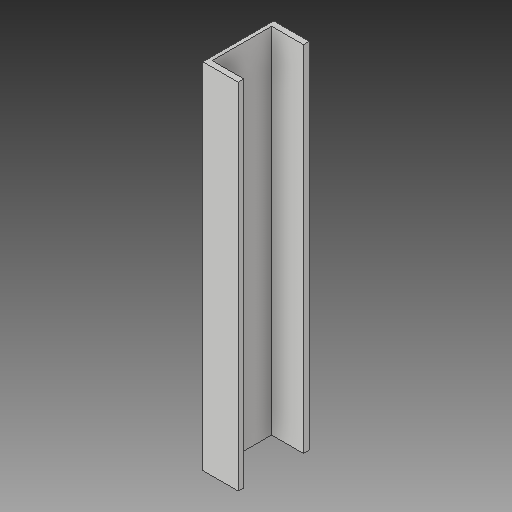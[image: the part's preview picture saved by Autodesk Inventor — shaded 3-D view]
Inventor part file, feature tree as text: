
AUTODESK INVENTOR PART (.ipt)
format: ipt  version: 2019 (Build 230136000, 136)  size: 88,064 bytes
history: native  units: in
note: dims shown in document units (in); Inventor stores cm internally (conversion verified against a paired STEP export)
features: other x3, sketch x1
ambient origin geometry x8: Origin, YZ Plane, XZ Plane, XY Plane, X Axis, Y Axis, Z Axis, Center Point
bodies: Solid1 (feature_tree)
feature tree (4):
  other  "Channel1_MIR_MIR1.ipt"
  other  "Solid1::Channel1_MIR_MIR1.ipt"
  other  "TaggingFeature1"
  sketch  "Sketch1"  dims[d0=0.3937in]
